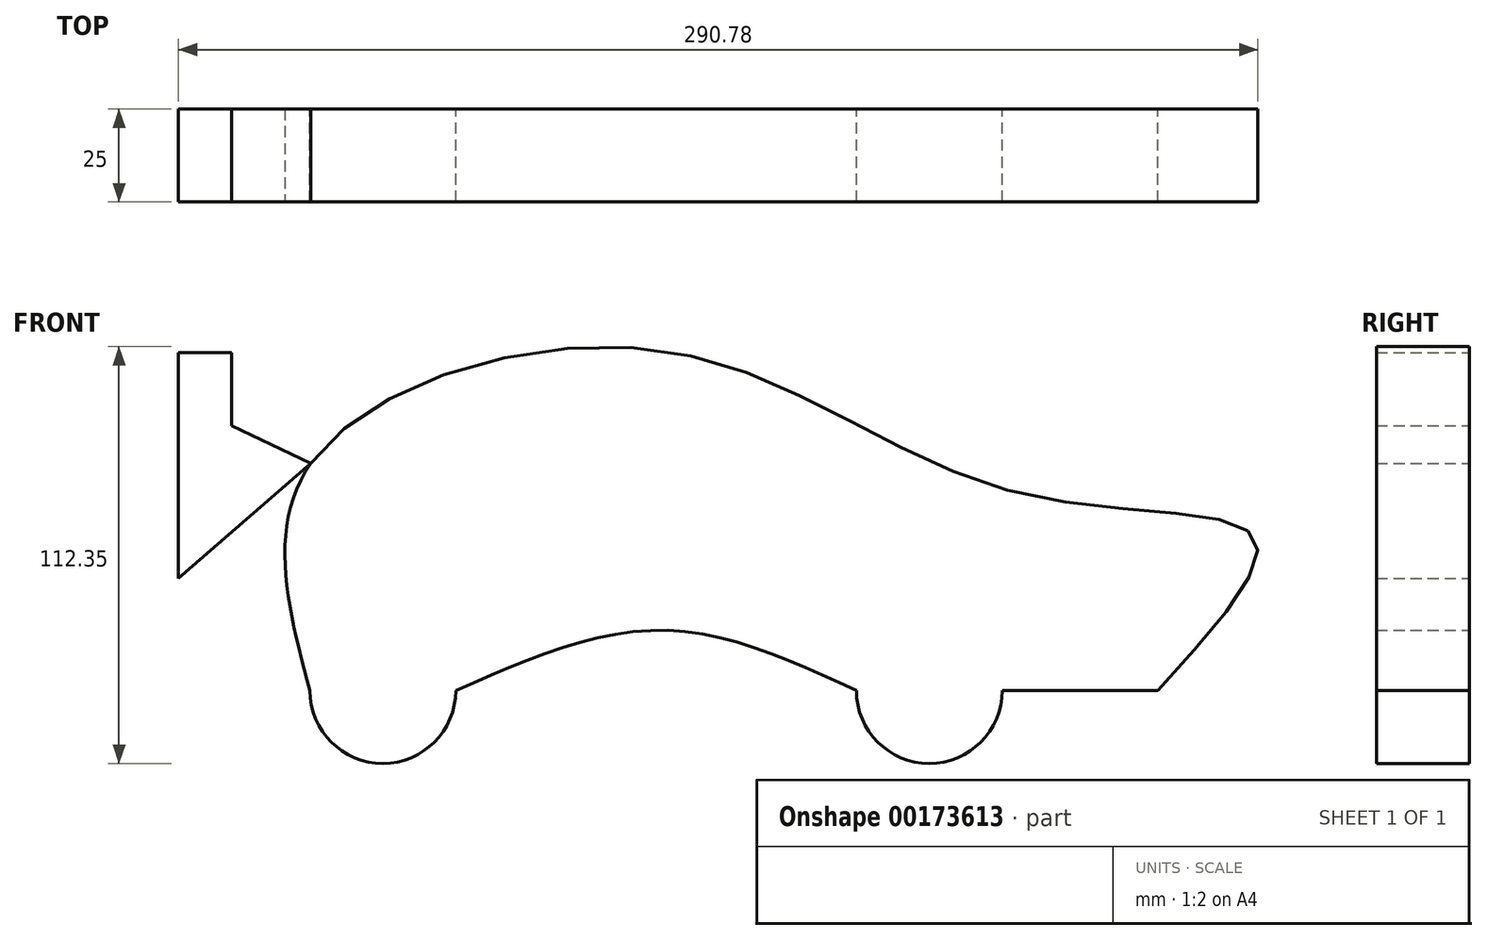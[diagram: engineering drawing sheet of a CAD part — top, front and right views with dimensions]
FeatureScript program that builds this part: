
annotation { "Feature Type Name" : "Feature", "Feature Type Description" : "" }
export const myFeature = defineFeature(function(context is Context, id is Id, definition is map)
    precondition{}
    {
        {
            var Q0;
            Q0=qCreatedBy(makeId("Front.planeOp"),FACE);
            var sketch = newSketch(context, id + "F0", { "sketchPlane" : qUnion([Q0])});
            skCircle(sketch, "E0", {"center": v(-92.14, -41.15) * mm, "radius": 19.63 * mm});
            skCircle(sketch, "E1", {"center": v(55.08, -41.15) * mm, "radius": 19.63 * mm});
            skFitSpline(sketch, "E2", {"points": [v(-111.77, -41.15) * mm, v(-111.55, 20.09) * mm, v(-16.77, 50.5) * mm, v(78.4, 12.29) * mm, v(142.75, 0) * mm, v(116.62, -41.15) * mm], "startDerivative": vector(-97.23, 363.86) * mm, "endDerivative": vector(-283.64, -309.6) * mm});
            skLineSegment(sketch, "E3", {"start": v(116.62, -41.15) * mm, "end": v(74.71, -41.15) * mm});
            skCircle(sketch, "E4", {"center": v(-92.14, -41.15) * mm, "radius": 12.5 * mm});
            skCircle(sketch, "E5", {"center": v(55.08, -41.15) * mm, "radius": 12.5 * mm});
            skFitSpline(sketch, "E6", {"points": [v(-72.5, -41.15) * mm, v(-16.99, -24.88) * mm, v(35.45, -41.15) * mm], "startDerivative": vector(110.45, 48.6) * mm, "endDerivative": vector(105.44, -49.02) * mm});
            skLineSegment(sketch, "E7", {"start": v(-111.55, 20.09) * mm, "end": v(-132.9, 30.25) * mm});
            skLineSegment(sketch, "E8", {"start": v(-132.9, 30.25) * mm, "end": v(-132.9, 49.91) * mm});
            skLineSegment(sketch, "E9", {"start": v(-132.9, 49.91) * mm, "end": v(-147.2, 49.91) * mm});
            skLineSegment(sketch, "E10", {"start": v(-147.2, 49.91) * mm, "end": v(-147.2, -10.88) * mm});
            skLineSegment(sketch, "E11", {"start": v(-147.2, -10.88) * mm, "end": v(-117.67, -19.08) * mm});
            skLineSegment(sketch, "E12", {"start": v(-132.9, 30.25) * mm, "end": v(-147.2, -10.88) * mm});
            skLineSegment(sketch, "E13", {"start": v(-111.55, 20.09) * mm, "end": v(-147.2, -10.88) * mm});
            skText(sketch, "E14", { "text": "RDX", "fontName": "OpenSans-BoldItalic.ttf"});
            const initialGuessF0  = {"E14": [-0.08564, 0.0039, 1, 0, 0.02107]};
            skSetInitialGuess(sketch, initialGuessF0);
            skSolve(sketch);
        }
        {
            var Q0;
            Q0 = qSketchRegion(id + "F0", true);
            var Q1;
            Q1=makeQuery(id+"F0.imprint","IMPRINT",FACE,{"disambiguationData":[TD([[makeQuery(id+"F0.imprint","IMPRINT",EDGE,{"derivedFrom":sQuery(id+"F0.wireOp",EDGE,"E4")}),1.0]])]});
            var Q2;
            Q2=makeQuery(id+"F0.imprint","IMPRINT",FACE,{"disambiguationData":[TD([[makeQuery(id+"F0.imprint","IMPRINT",EDGE,{"derivedFrom":sQuery(id+"F0.wireOp",EDGE,"E5")}),1.0]])]});
            var Q3;
            Q3=makeQuery(id+"F0.imprint","IMPRINT",FACE,{"disambiguationData":[TD([[makeQuery(id+"F0.imprint","IMPRINT",EDGE,{"derivedFrom":sQuery(id+"F0.wireOp",EDGE,"E4")}),-1.0]])]});
            var Q4;
            Q4=makeQuery(id+"F0.imprint","IMPRINT",FACE,{"disambiguationData":[TD([[makeQuery(id+"F0.imprint","IMPRINT",EDGE,{"derivedFrom":sQuery(id+"F0.wireOp",EDGE,"E5")}),-1.0]])]});
            var Q5;
            Q5=makeQuery(id+"F0.imprint","IMPRINT",FACE,{"disambiguationData":[TD([[makeQuery(id+"F0.imprint","IMPRINT",EDGE,{"derivedFrom":sQuery(id+"F0.wireOp",EDGE,"E14.sketch_text.stroke-0")}),-1.0]])]});
            var Q6;
            {var subQ0=sQuery(id+"F0.wireOp",EDGE,"E3");Q6=makeQuery(id+"F0.imprint","IMPRINT",FACE,{"disambiguationData":[TD([[makeQuery(id+"F0.imprint","IMPRINT",EDGE,{"derivedFrom":subQ0}),-1.0]])]});}
            var Q7;
            Q7=makeQuery(id+"F0.imprint","IMPRINT",FACE,{"disambiguationData":[TD([[makeQuery(id+"F0.imprint","IMPRINT",EDGE,{"derivedFrom":sQuery(id+"F0.wireOp",EDGE,"E14.sketch_text.stroke-0")}),1.0]])]});
            var Q8;
            Q8=makeQuery(id+"F0.imprint","IMPRINT",FACE,{"disambiguationData":[TD([[makeQuery(id+"F0.imprint","IMPRINT",EDGE,{"derivedFrom":sQuery(id+"F0.wireOp",EDGE,"E14.sketch_text.stroke-27")}),1.0]])]});
            var Q9;
            Q9=makeQuery(id+"F0.imprint","IMPRINT",FACE,{"disambiguationData":[TD([[makeQuery(id+"F0.imprint","IMPRINT",EDGE,{"derivedFrom":sQuery(id+"F0.wireOp",EDGE,"E14.sketch_text.stroke-35")}),-1.0]])]});
            var Q10;
            Q10=makeQuery(id+"F0.imprint","IMPRINT",FACE,{"disambiguationData":[TD([[makeQuery(id+"F0.imprint","IMPRINT",EDGE,{"derivedFrom":sQuery(id+"F0.wireOp",EDGE,"E14.sketch_text.stroke-19")}),-1.0]])]});
            extrude(context, id + "F1", {"entities" : qUnion([Q0, Q1, Q2, Q3, Q4, Q5, Q6, Q7, Q8, Q9, Q10]), "depth" : 25 * mm});
        }
    });
